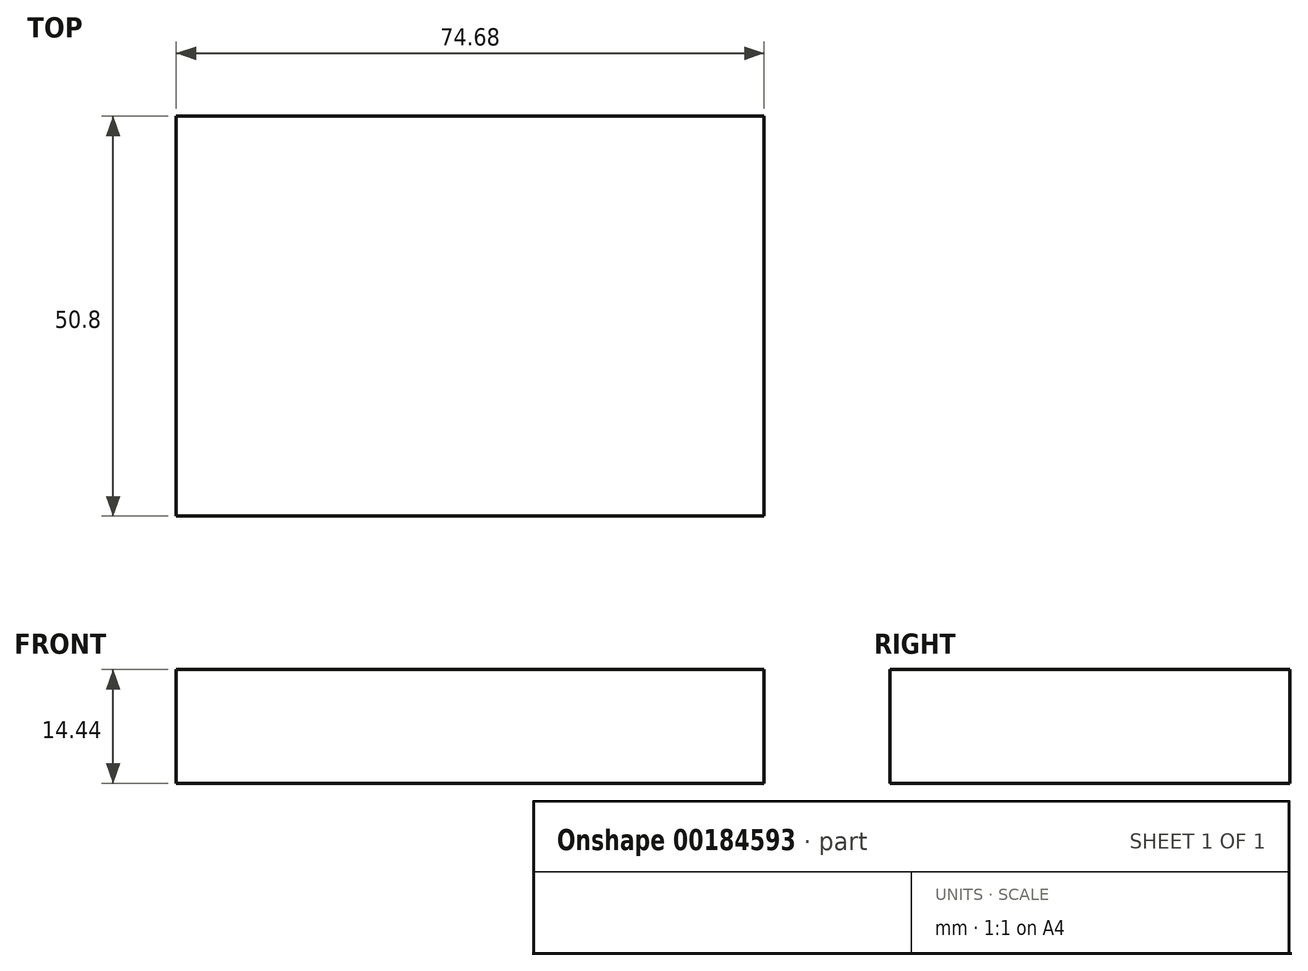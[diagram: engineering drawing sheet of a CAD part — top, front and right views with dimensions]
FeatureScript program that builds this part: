
annotation { "Feature Type Name" : "Feature", "Feature Type Description" : "" }
export const myFeature = defineFeature(function(context is Context, id is Id, definition is map)
    precondition{}
    {
        {
            var Q0;
            Q0=qCreatedBy(makeId("Front.planeOp"),FACE);
            var sketch = newSketch(context, id + "F0", { "sketchPlane" : qUnion([Q0])});
            skLineSegment(sketch, "E0.bottom", {"start": v(-32.95, 29.8) * mm, "end": v(41.73, 29.8) * mm});
            skLineSegment(sketch, "E0.top", {"start": v(-32.95, 15.37) * mm, "end": v(41.73, 15.37) * mm});
            skLineSegment(sketch, "E0.left", {"start": v(-32.95, 29.8) * mm, "end": v(-32.95, 15.37) * mm});
            skLineSegment(sketch, "E0.right", {"start": v(41.73, 29.8) * mm, "end": v(41.73, 15.37) * mm});
            skSolve(sketch);
        }
        {
            var Q0;
            Q0 = qSketchRegion(id + "F0", true);
            extrude(context, id + "F1", {"entities" : qUnion([Q0]), "depth" : 25.4 * mm, "hasSecondDirection" : true, "secondDirectionOppositeDirection" : true, "secondDirectionDepth" : 25.4 * mm});
        }
    });
